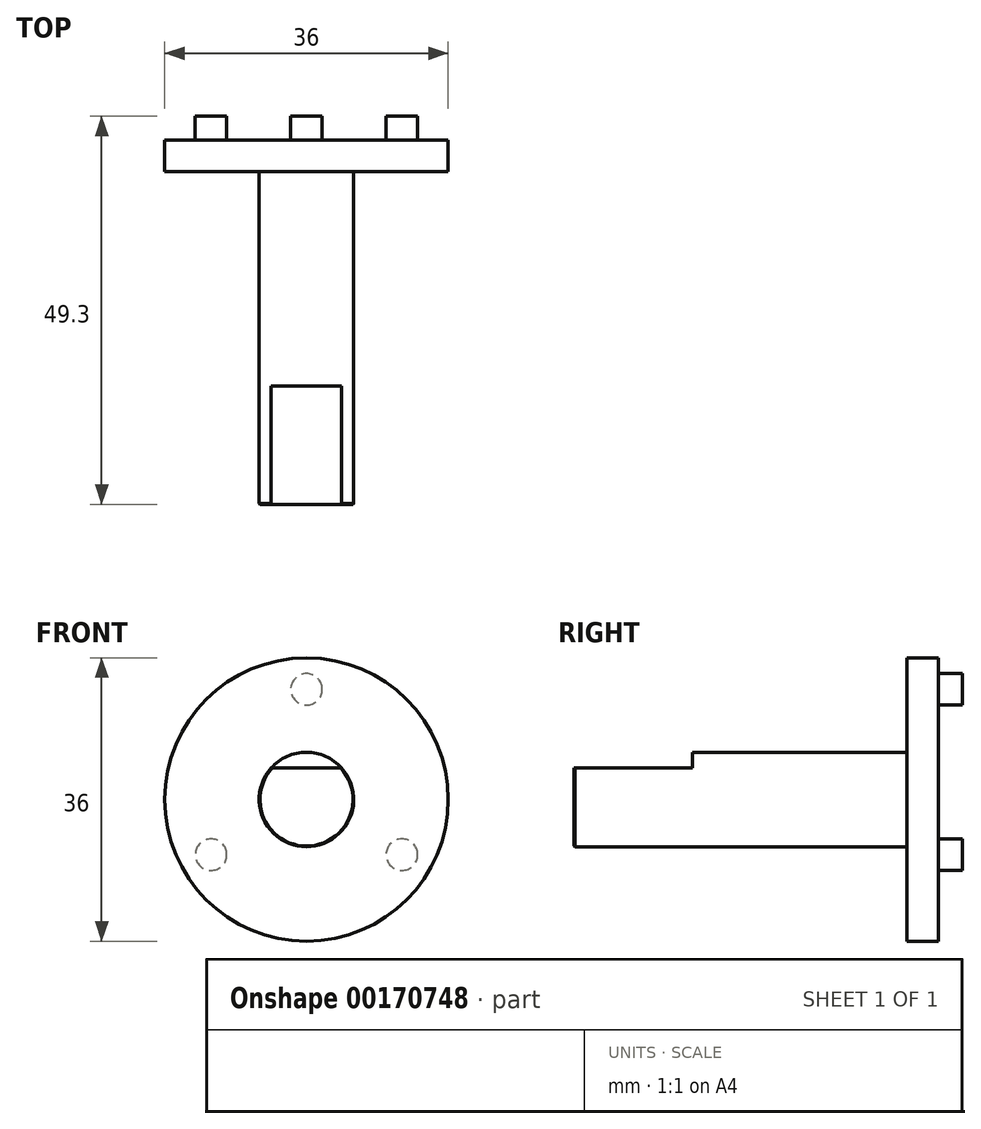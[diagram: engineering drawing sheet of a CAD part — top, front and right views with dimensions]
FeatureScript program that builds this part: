
annotation { "Feature Type Name" : "Feature", "Feature Type Description" : "" }
export const myFeature = defineFeature(function(context is Context, id is Id, definition is map)
    precondition{}
    {
        {
            var Q0;
            Q0=qCreatedBy(makeId("Front.planeOp"),FACE);
            var sketch = newSketch(context, id + "F0", { "sketchPlane" : qUnion([Q0])});
            skCircle(sketch, "E0", {"center": v(0, 0) * mm, "radius": 6 * mm});
            skSolve(sketch);
        }
        {
            var Q0;
            Q0=qSketchRegion(id+"F0",true);
            extrude(context, id + "F1", {"entities" : qUnion([Q0]), "flatOperationType" : FlatOperationType.REMOVE, "offsetDistance" : 25 * mm, "depth" : 42.3 * mm, "domain" : OperationDomain.MODEL});
        }
        {
            var Q0;
            Q0=makeQuery(id+"F1.opExtrude","CAP_FACE",FACE,{"disambiguationData":[OSD([sQuery(id+"F0.wireOp",EDGE,"E0")])],"isStart":false});
            var sketch = newSketch(context, id + "F2", { "sketchPlane" : qUnion([Q0])});
            skLineSegment(sketch, "E1", {"start": v(-4.47, 4) * mm, "end": v(4.47, 4) * mm});
            skArc(sketch, "E2", {"start": v(-4.47, 4) * mm, "mid": v(0, 6) * mm, "end": v(4.47, 4) * mm});
            skSolve(sketch);
        }
        {
            var Q0;
            Q0=qSketchRegion(id+"F2",true);
            extrude(context, id + "F3", {"entities" : qUnion([Q0]), "operationType" : NewBodyOperationType.REMOVE, "oppositeDirection" : true, "depth" : 15 * mm});
        }
        {
            var Q0;
            Q0=makeQuery(id+"F1.opExtrude","CAP_EDGE",EDGE,{"disambiguationData":[OSD([sQuery(id+"F0.wireOp",EDGE,"E0")])],"isStart":false});
            var Q1;
            {var subQ0=sQuery(id+"F2.wireOp",EDGE,"E2");var subQ1=sQuery(id+"F2.wireOp",EDGE,"E1");var subQ2=sQuery(id+"F0.wireOp",EDGE,"E0");Q1=makeQuery(id+"F3.boolean.opBoolean","COPY",EDGE,{"derivedFrom":makeQuery(id+"F3.opExtrude","SWEPT_EDGE",EDGE,{"disambiguationData":[OSD([subQ2,subQ1,subQ0]),TDD([makeQuery(id+"F2.imprint","INTERSECT",VERTEX,{"disambiguationData":[OD(1.0)],"derivedFrom":[makeQuery(id+"F1.opExtrude","CAP_EDGE",EDGE,{"disambiguationData":[OSD([subQ2])],"isStart":false}),subQ1,subQ0]})])]})});}
            var Q2;
            {var subQ0=sQuery(id+"F2.wireOp",EDGE,"E2");var subQ1=sQuery(id+"F2.wireOp",EDGE,"E1");var subQ2=sQuery(id+"F0.wireOp",EDGE,"E0");Q2=makeQuery(id+"F3.boolean.opBoolean","COPY",EDGE,{"derivedFrom":makeQuery(id+"F3.opExtrude","SWEPT_EDGE",EDGE,{"disambiguationData":[OSD([subQ2,subQ1,subQ0]),TDD([makeQuery(id+"F2.imprint","INTERSECT",VERTEX,{"disambiguationData":[OD(0.0)],"derivedFrom":[makeQuery(id+"F1.opExtrude","CAP_EDGE",EDGE,{"disambiguationData":[OSD([subQ2])],"isStart":false}),subQ1,subQ0]})])]})});}
            var Q3;
            Q3=makeQuery(id+"F3.boolean.opBoolean","COPY",EDGE,{"derivedFrom":makeQuery(id+"F3.opExtrude","CAP_EDGE",EDGE,{"disambiguationData":[OSD([sQuery(id+"F2.wireOp",EDGE,"E2")])],"isStart":false})});
            chamfer(context, id + "F4", {"entities" : qUnion([Q0, Q1, Q2, Q3]), "width" : 0.1 * mm, "tangentPropagation" : true});
        }
        {
            var Q0;
            Q0=makeQuery(id+"F1.opExtrude","CAP_FACE",FACE,{"disambiguationData":[OSD([sQuery(id+"F0.wireOp",EDGE,"E0")])],"isStart":true});
            var sketch = newSketch(context, id + "F5", { "sketchPlane" : qUnion([Q0])});
            skCircle(sketch, "E3", {"center": v(0, 0) * mm, "radius": 18 * mm});
            skSolve(sketch);
        }
        {
            var Q0;
            Q0=qSketchRegion(id+"F5",true);
            extrude(context, id + "F6", {"entities" : qUnion([Q0]), "operationType" : NewBodyOperationType.ADD, "depth" : 4 * mm});
        }
        {
            var Q0;
            Q0=makeQuery(id+"F6.opExtrude","CAP_FACE",FACE,{"disambiguationData":[OSD([sQuery(id+"F5.wireOp",EDGE,"E3")])],"isStart":false});
            var sketch = newSketch(context, id + "F7", { "sketchPlane" : qUnion([Q0])});
            skCircle(sketch, "E4", {"center": v(0, 0) * mm, "radius": 14 * mm, "construction": true});
            skLineSegment(sketch, "E5", {"start": v(0, 0) * mm, "end": v(0, 18) * mm, "construction": true});
            skCircle(sketch, "E6", {"center": v(0, 14) * mm, "radius": 2 * mm});
            skCircle(sketch, "E7.1.0", {"center": v(-12.12, -7) * mm, "radius": 2 * mm});
            skCircle(sketch, "E7.2.0", {"center": v(12.12, -7) * mm, "radius": 2 * mm});
            skSolve(sketch);
        }
        {
            var Q0;
            Q0=qSketchRegion(id+"F7",true);
            extrude(context, id + "F8", {"entities" : qUnion([Q0]), "operationType" : NewBodyOperationType.ADD, "depth" : 3 * mm});
        }
    });
